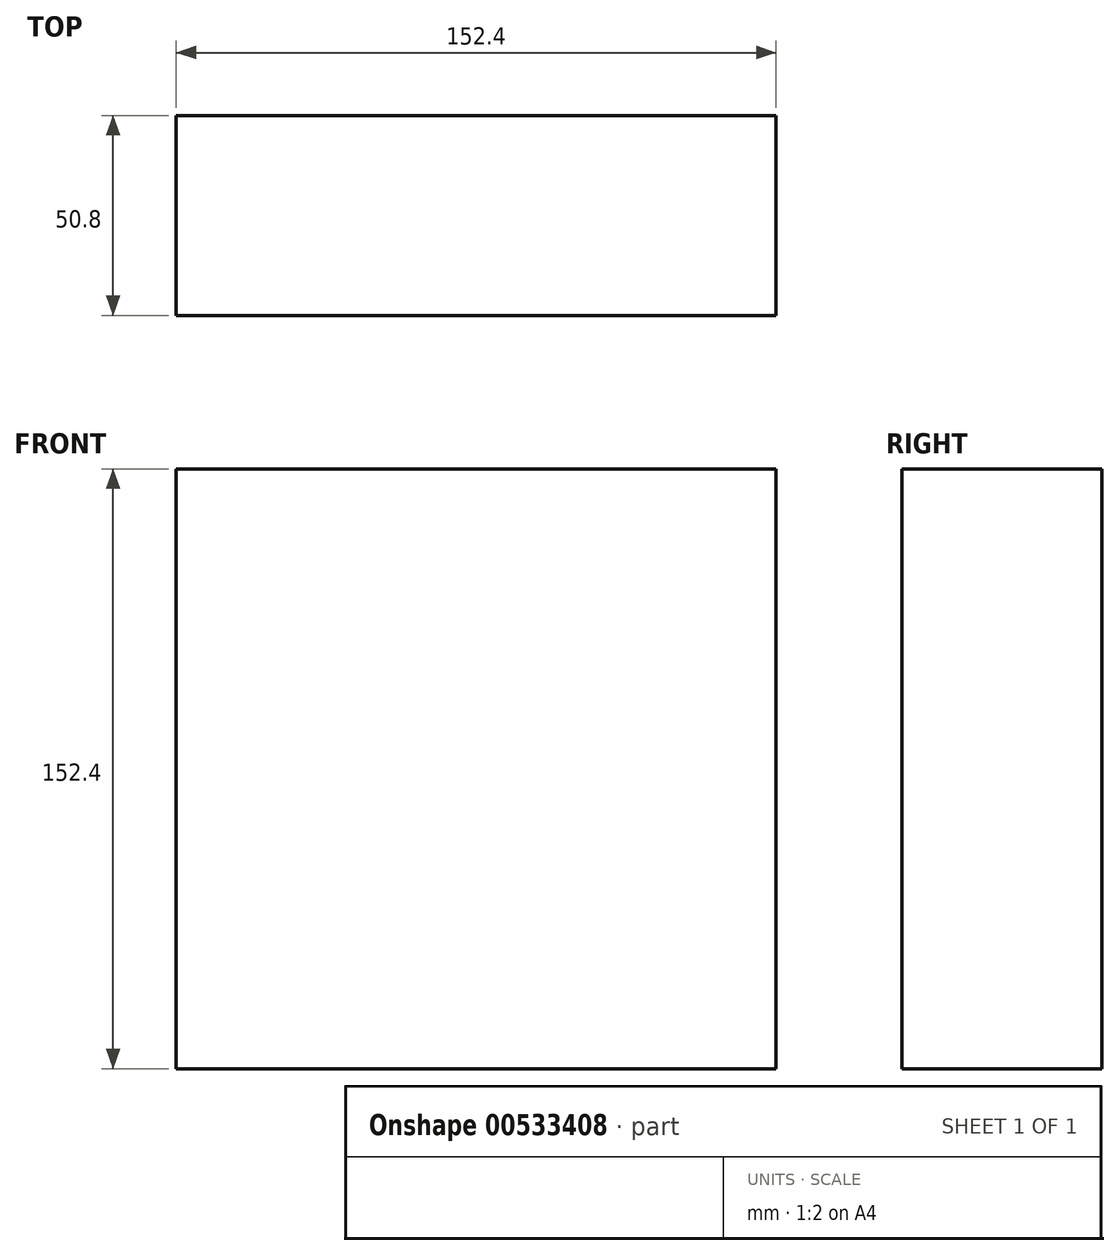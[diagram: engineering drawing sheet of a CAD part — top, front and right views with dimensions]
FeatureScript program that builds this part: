
annotation { "Feature Type Name" : "Feature", "Feature Type Description" : "" }
export const myFeature = defineFeature(function(context is Context, id is Id, definition is map)
    precondition{}
    {
        {
            var Q0;
            Q0=qCreatedBy(makeId("Front.planeOp"),FACE);
            var sketch = newSketch(context, id + "F0", { "sketchPlane" : qUnion([Q0])});
            skLineSegment(sketch, "E0.bottom", {"start": v(-74.86, -86.01) * mm, "end": v(77.54, -86.01) * mm});
            skLineSegment(sketch, "E0.top", {"start": v(-74.86, 66.39) * mm, "end": v(77.54, 66.39) * mm});
            skLineSegment(sketch, "E0.left", {"start": v(-74.86, -86.01) * mm, "end": v(-74.86, 66.39) * mm});
            skLineSegment(sketch, "E0.right", {"start": v(77.54, -86.01) * mm, "end": v(77.54, 66.39) * mm});
            skSolve(sketch);
        }
        {
            var Q0;
            Q0 = qSketchRegion(id + "F0", true);
            var Q1;
            Q1 = qSketchRegion(id + "F2", true);
            extrude(context, id + "F1", {"entities" : qUnion([Q0, Q1]), "depth" : 50.8 * mm, "offsetDistance" : 25.4 * mm});
        }
    });
